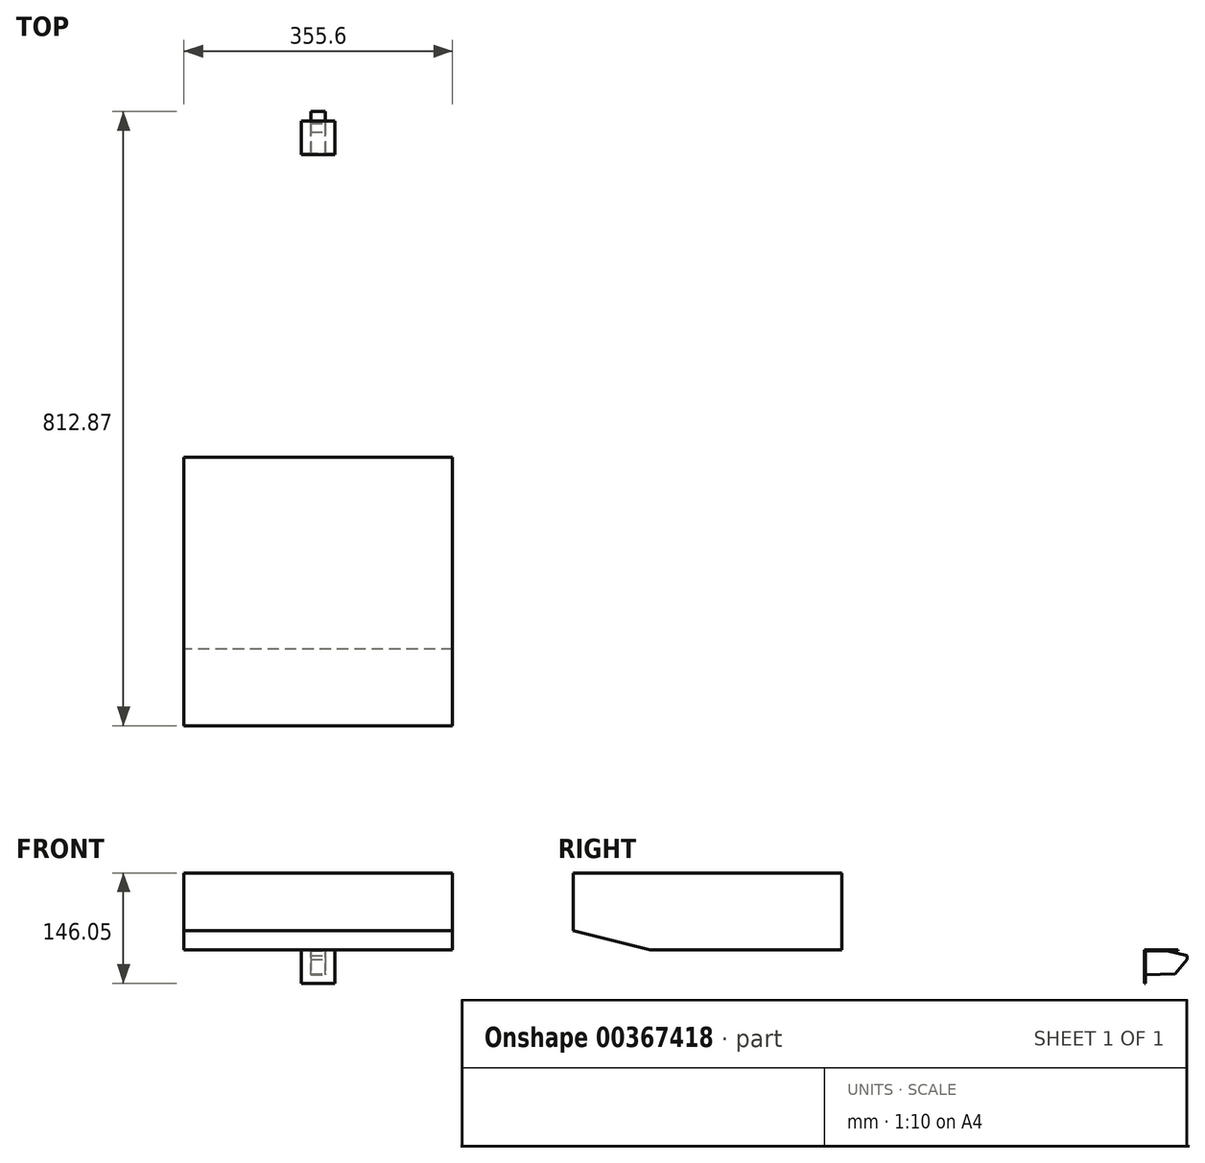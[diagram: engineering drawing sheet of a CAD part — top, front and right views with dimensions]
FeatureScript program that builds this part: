
annotation { "Feature Type Name" : "Feature", "Feature Type Description" : "" }
export const myFeature = defineFeature(function(context is Context, id is Id, definition is map)
    precondition{}
    {
        {
            var Q0;
            Q0=qCreatedBy(makeId("Right.planeOp"),FACE);
            var sketch = newSketch(context, id + "F0", { "sketchPlane" : qUnion([Q0])});
            skLineSegment(sketch, "E0", {"start": v(0, 0) * mm, "end": v(44.45, 0) * mm});
            skLineSegment(sketch, "E1", {"start": v(44.45, -1.52) * mm, "end": v(1.52, -1.52) * mm});
            skLineSegment(sketch, "E2", {"start": v(1.52, -1.52) * mm, "end": v(1.52, -44.45) * mm});
            skLineSegment(sketch, "E3", {"start": v(1.52, -44.45) * mm, "end": v(0, -44.45) * mm});
            skLineSegment(sketch, "E4", {"start": v(0, -44.45) * mm, "end": v(0, 0) * mm});
            skLineSegment(sketch, "E5", {"start": v(44.45, 0) * mm, "end": v(44.45, -1.52) * mm});
            skSolve(sketch);
        }
        {
            var Q0;
            Q0 = qSketchRegion(id + "F0", true);
            extrude(context, id + "F1", {"entities" : qUnion([Q0]), "endBound" : BoundingType.SYMMETRIC, "depth" : 44.45 * mm});
        }
        {
            var Q0;
            Q0=qCreatedBy(makeId("Right.planeOp"),FACE);
            var sketch = newSketch(context, id + "F2", { "sketchPlane" : qUnion([Q0])});
            skLineSegment(sketch, "E6", {"start": v(1.52, -1.52) * mm, "end": v(30.1, -1.52) * mm});
            skLineSegment(sketch, "E7", {"start": v(30.1, -1.52) * mm, "end": v(57.15, -7.92) * mm});
            skLineSegment(sketch, "E8", {"start": v(57.15, -7.92) * mm, "end": v(57.15, -12.69) * mm});
            skLineSegment(sketch, "E9", {"start": v(57.15, -12.69) * mm, "end": v(41.28, -31.75) * mm});
            skLineSegment(sketch, "E10", {"start": v(41.28, -31.75) * mm, "end": v(1.52, -33.32) * mm});
            skLineSegment(sketch, "E11", {"start": v(1.52, -33.32) * mm, "end": v(1.52, -1.52) * mm});
            skSolve(sketch);
        }
        {
            var Q0;
            Q0 = qSketchRegion(id + "F2", true);
            extrude(context, id + "F3", {"entities" : qUnion([Q0]), "operationType" : NewBodyOperationType.ADD, "endBound" : BoundingType.SYMMETRIC, "oppositeDirection" : true, "depth" : 19.05 * mm});
        }
        {
            var Q0;
            Q0=qCreatedBy(makeId("Top.planeOp"),FACE);
            var sketch = newSketch(context, id + "F4", { "sketchPlane" : qUnion([Q0])});
            skLineSegment(sketch, "E12.bottom", {"start": v(177.8, -400.12) * mm, "end": v(-177.8, -400.12) * mm});
            skLineSegment(sketch, "E12.top", {"start": v(177.8, -755.72) * mm, "end": v(-177.8, -755.72) * mm});
            skLineSegment(sketch, "E12.left", {"start": v(177.8, -400.12) * mm, "end": v(177.8, -755.72) * mm});
            skLineSegment(sketch, "E12.right", {"start": v(-177.8, -400.12) * mm, "end": v(-177.8, -755.72) * mm});
            skPoint(sketch, "E12.middle", {"position": v(0, -577.92) * mm});
            skLineSegment(sketch, "E13", {"start": v(0, -577.92) * mm, "end": v(0, 0) * mm});
            skSolve(sketch);
        }
        {
            var Q0;
            Q0 = qSketchRegion(id + "F4", true);
            extrude(context, id + "F5", {"entities" : qUnion([Q0]), "depth" : 101.6 * mm});
        }
        {
            var Q0;
            Q0=makeQuery(id+"F5.opExtrude","SWEPT_FACE",FACE,{"disambiguationData":[OSD([sQuery(id+"F4.wireOp",EDGE,"E12.right")])]});
            var sketch = newSketch(context, id + "F6", { "sketchPlane" : qUnion([Q0])});
            skLineSegment(sketch, "E14", {"start": v(755.72, 25.4) * mm, "end": v(654.12, 0) * mm});
            skLineSegment(sketch, "E15", {"start": v(654.12, 0) * mm, "end": v(755.72, 0) * mm});
            skLineSegment(sketch, "E16", {"start": v(755.72, 0) * mm, "end": v(755.72, 25.4) * mm});
            skSolve(sketch);
        }
        {
            var Q0;
            Q0 = qSketchRegion(id + "F6", true);
            extrude(context, id + "F7", {"entities" : qUnion([Q0]), "operationType" : NewBodyOperationType.REMOVE, "endBound" : BoundingType.UP_TO_NEXT, "oppositeDirection" : true, "depth" : 25.4 * mm});
        }
    });
